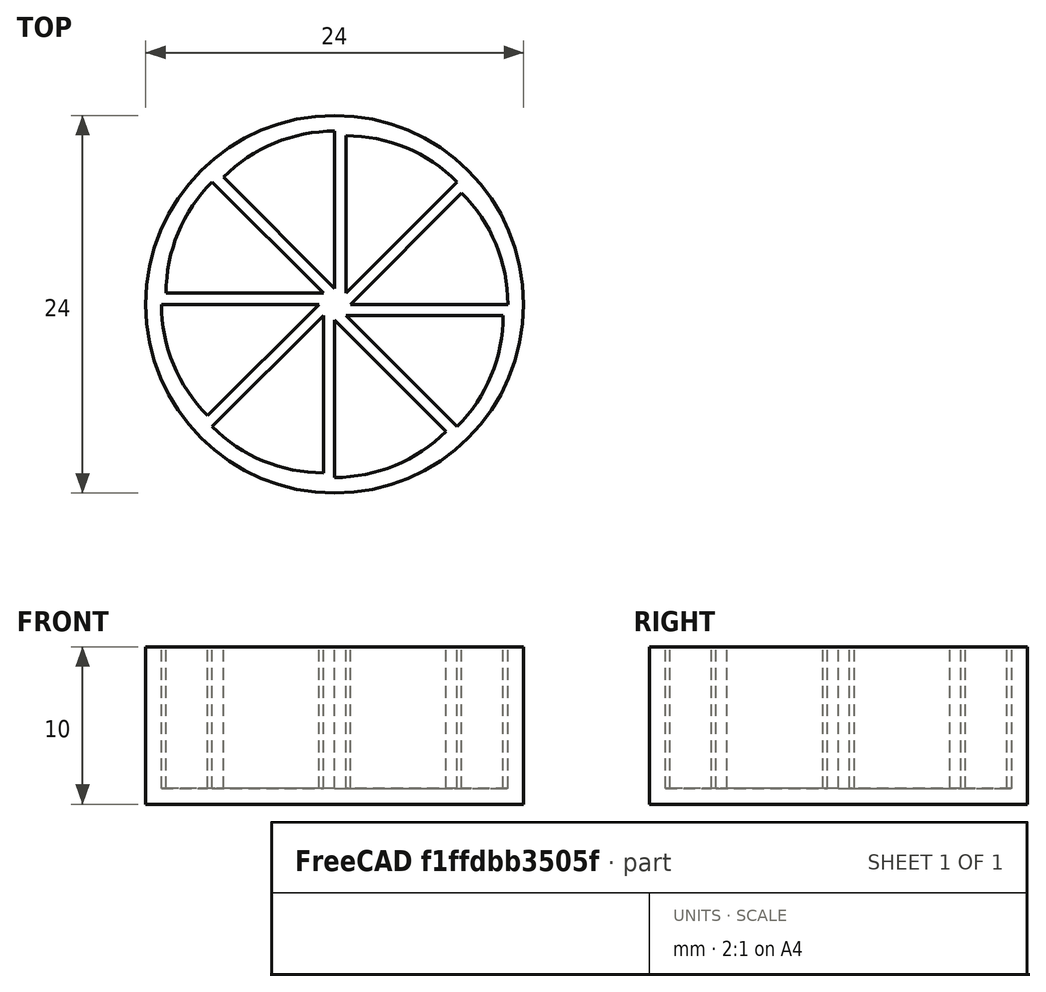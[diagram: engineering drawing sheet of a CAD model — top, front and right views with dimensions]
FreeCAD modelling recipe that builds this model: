
FCSTD DOCUMENT  (FreeCAD 0.18R16146 (Git))
Label: trivial_dani
License: All rights reserved
LicenseURL: http://en.wikipedia.org/wiki/All_rights_reserved
objects: Part::Cylinder×2, Part::FeaturePython×1, Part::Cut×1
note: 4 computed .brp shape members not serialized (recipe doc carries the construction recipe); baked Part::Feature solids carry a one-line shape summary decoded from their .brp

FEATURE [Part::Cylinder] Cylinder  label="Cilindro"
  Angle = 360
  AttacherType = Attacher::AttachEngine3D
  Height = 10
  Radius = 12
FEATURE [Part::Cylinder] Cylinder001  label="quesito"
  Angle = 45
  AttacherType = Attacher::AttachEngine3D
  Height = 10
  Placement = pos=(1,0,0) rot=(0,0,1;0rad)
  Radius = 10
FEATURE [Part::FeaturePython] Array  # Draft array (typed FeaturePython)
  Angle = 360
  ArrayType = 1
  Axis = (0,0,1)
  Base = -> Cylinder001
  Center = (0,0,0)
  Fuse = false
  IntervalAxis = (0,0,0)
  IntervalX = (1,0,0)
  IntervalY = (0,1,0)
  IntervalZ = (0,0,1)
  NumberPolar = 8
  NumberX = 2
  NumberY = 2
  NumberZ = 1
  Placement = pos=(0,0,1) rot=(0,0,1;0rad)
FEATURE [Part::Cut] Cut
  Base = -> Cylinder
  Refine = true
  Tool = -> Array
